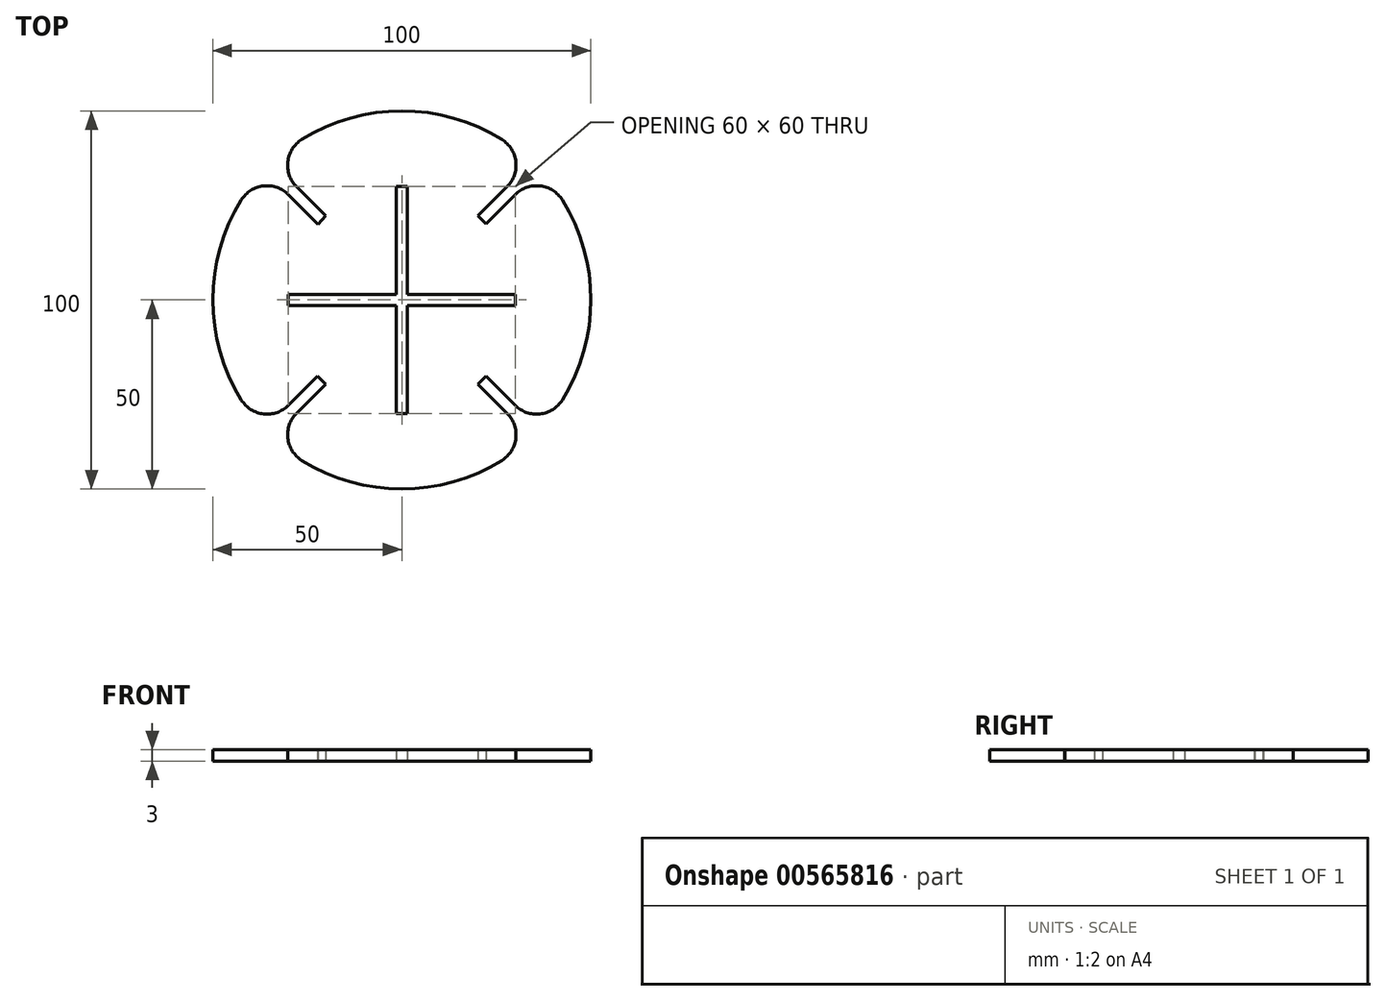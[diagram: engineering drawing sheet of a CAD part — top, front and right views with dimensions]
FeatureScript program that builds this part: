
annotation { "Feature Type Name" : "Feature", "Feature Type Description" : "" }
export const myFeature = defineFeature(function(context is Context, id is Id, definition is map)
    precondition{}
    {
        {
            var Q0;
            Q0=qCreatedBy(makeId("Top.planeOp"),FACE);
            var sketch = newSketch(context, id + "F0", { "sketchPlane" : qUnion([Q0])});
            skArc(sketch, "E0", {"start": v(-42.44, 26.44) * mm, "mid": v(-50, 0) * mm, "end": v(-42.44, -26.44) * mm});
            skLineSegment(sketch, "E1.bottom", {"start": v(1.5, 30) * mm, "end": v(-1.5, 30) * mm});
            skLineSegment(sketch, "E1.top", {"start": v(1.5, -30) * mm, "end": v(-1.5, -30) * mm});
            skLineSegment(sketch, "E1.left", {"start": v(1.5, 30) * mm, "end": v(1.5, -30) * mm});
            skLineSegment(sketch, "E1.right", {"start": v(-1.5, 30) * mm, "end": v(-1.5, -30) * mm});
            skLineSegment(sketch, "E2.bottom", {"start": v(-30, 1.5) * mm, "end": v(30, 1.5) * mm});
            skLineSegment(sketch, "E2.top", {"start": v(-30, -1.5) * mm, "end": v(30, -1.5) * mm});
            skLineSegment(sketch, "E2.left", {"start": v(-30, 1.5) * mm, "end": v(-30, -1.5) * mm});
            skLineSegment(sketch, "E2.right", {"start": v(30, 1.5) * mm, "end": v(30, -1.5) * mm});
            skLineSegment(sketch, "E3", {"start": v(-35.36, -35.36) * mm, "end": v(0, 0) * mm, "construction": true});
            skLineSegment(sketch, "E4", {"start": v(0, 0) * mm, "end": v(35.36, -35.36) * mm, "construction": true});
            skLineSegment(sketch, "E5", {"start": v(0, 0) * mm, "end": v(-35.36, 35.36) * mm, "construction": true});
            skLineSegment(sketch, "E6", {"start": v(0, 0) * mm, "end": v(35.36, 35.36) * mm, "construction": true});
            skLineSegment(sketch, "E7", {"start": v(-27.87, -29.99) * mm, "end": v(-20.15, -22.27) * mm});
            skLineSegment(sketch, "E8.MirrorCS", {"start": v(-29.99, -27.87) * mm, "end": v(-22.27, -20.15) * mm});
            skLineSegment(sketch, "E9", {"start": v(-27.87, 29.99) * mm, "end": v(-20.19, 22.31) * mm});
            skLineSegment(sketch, "E10.MirrorCS", {"start": v(-29.99, 27.87) * mm, "end": v(-22.11, 19.99) * mm});
            skLineSegment(sketch, "E11", {"start": v(-20.15, -22.27) * mm, "end": v(-22.27, -20.15) * mm});
            skLineSegment(sketch, "E12.trimOffspring", {"start": v(-3.62, -1.5) * mm, "end": v(1.5, 3.62) * mm});
            skLineSegment(sketch, "E13.trimOffspring", {"start": v(-1.5, -3.62) * mm, "end": v(3.62, 1.5) * mm});
            skLineSegment(sketch, "E14", {"start": v(20.15, -22.27) * mm, "end": v(22.27, -20.15) * mm});
            skLineSegment(sketch, "E15", {"start": v(22.27, 20.15) * mm, "end": v(20.15, 22.27) * mm});
            skLineSegment(sketch, "E16", {"start": v(-22.11, 19.99) * mm, "end": v(-20.19, 22.31) * mm});
            skLineSegment(sketch, "E17.trimOffspring", {"start": v(-3.62, 1.5) * mm, "end": v(1.5, -3.62) * mm});
            skLineSegment(sketch, "E18.trimOffspring", {"start": v(-1.5, 3.62) * mm, "end": v(3.62, -1.5) * mm});
            skLineSegment(sketch, "E19.trimOffspring", {"start": v(20.15, -22.27) * mm, "end": v(27.87, -29.99) * mm});
            skLineSegment(sketch, "E20.trimOffspring", {"start": v(22.27, -20.15) * mm, "end": v(29.99, -27.87) * mm});
            skLineSegment(sketch, "E21.trimOffspring", {"start": v(22.27, 20.15) * mm, "end": v(29.99, 27.87) * mm});
            skLineSegment(sketch, "E22.trimOffspring", {"start": v(20.15, 22.27) * mm, "end": v(27.87, 29.99) * mm});
            skArc(sketch, "E23.trimOffspring", {"start": v(-26.44, -42.44) * mm, "mid": v(0, -50) * mm, "end": v(26.44, -42.44) * mm});
            skArc(sketch, "E24.trimOffspring", {"start": v(42.44, -26.44) * mm, "mid": v(50, 0) * mm, "end": v(42.44, 26.44) * mm});
            skArc(sketch, "E25.trimOffspring", {"start": v(26.44, 42.44) * mm, "mid": v(0, 50) * mm, "end": v(-26.44, 42.44) * mm});
            skPoint(sketch, "E26.visualSharp", {"position": v(-36.4, 34.28) * mm});
            skArc(sketch, "E26.filletArc", {"start": v(-29.99, 27.87) * mm, "mid": v(-36.56, 30.16) * mm, "end": v(-42.44, 26.44) * mm});
            skPoint(sketch, "E27.visualSharp", {"position": v(-34.28, 36.4) * mm});
            skArc(sketch, "E27.filletArc", {"start": v(-26.44, 42.44) * mm, "mid": v(-30.16, 36.56) * mm, "end": v(-27.87, 29.99) * mm});
            skPoint(sketch, "E28.visualSharp", {"position": v(-36.4, -34.28) * mm});
            skArc(sketch, "E28.filletArc", {"start": v(-42.44, -26.44) * mm, "mid": v(-36.56, -30.16) * mm, "end": v(-29.99, -27.87) * mm});
            skPoint(sketch, "E29.visualSharp", {"position": v(-34.28, -36.4) * mm});
            skArc(sketch, "E29.filletArc", {"start": v(-27.87, -29.99) * mm, "mid": v(-30.16, -36.56) * mm, "end": v(-26.44, -42.44) * mm});
            skPoint(sketch, "E30.visualSharp", {"position": v(34.28, -36.4) * mm});
            skArc(sketch, "E30.filletArc", {"start": v(26.44, -42.44) * mm, "mid": v(30.16, -36.56) * mm, "end": v(27.87, -29.99) * mm});
            skPoint(sketch, "E31.visualSharp", {"position": v(36.4, -34.28) * mm});
            skArc(sketch, "E31.filletArc", {"start": v(29.99, -27.87) * mm, "mid": v(36.56, -30.16) * mm, "end": v(42.44, -26.44) * mm});
            skPoint(sketch, "E32.visualSharp", {"position": v(36.4, 34.28) * mm});
            skArc(sketch, "E32.filletArc", {"start": v(42.44, 26.44) * mm, "mid": v(36.56, 30.16) * mm, "end": v(29.99, 27.87) * mm});
            skPoint(sketch, "E33.visualSharp", {"position": v(34.28, 36.4) * mm});
            skArc(sketch, "E33.filletArc", {"start": v(27.87, 29.99) * mm, "mid": v(30.16, 36.56) * mm, "end": v(26.44, 42.44) * mm});
            skSolve(sketch);
        }
        {
            var Q0;
            Q0=makeQuery(id+"F0.imprint","IMPRINT",FACE,{"disambiguationData":[TD([[makeQuery(id+"F0.imprint","IMPRINT",EDGE,{"derivedFrom":sQuery(id+"F0.wireOp",EDGE,"E0")}),1.0]])]});
            extrude(context, id + "F1", {"entities" : qUnion([Q0]), "depth" : 3 * mm, "offsetDistance" : 25 * mm});
        }
    });
